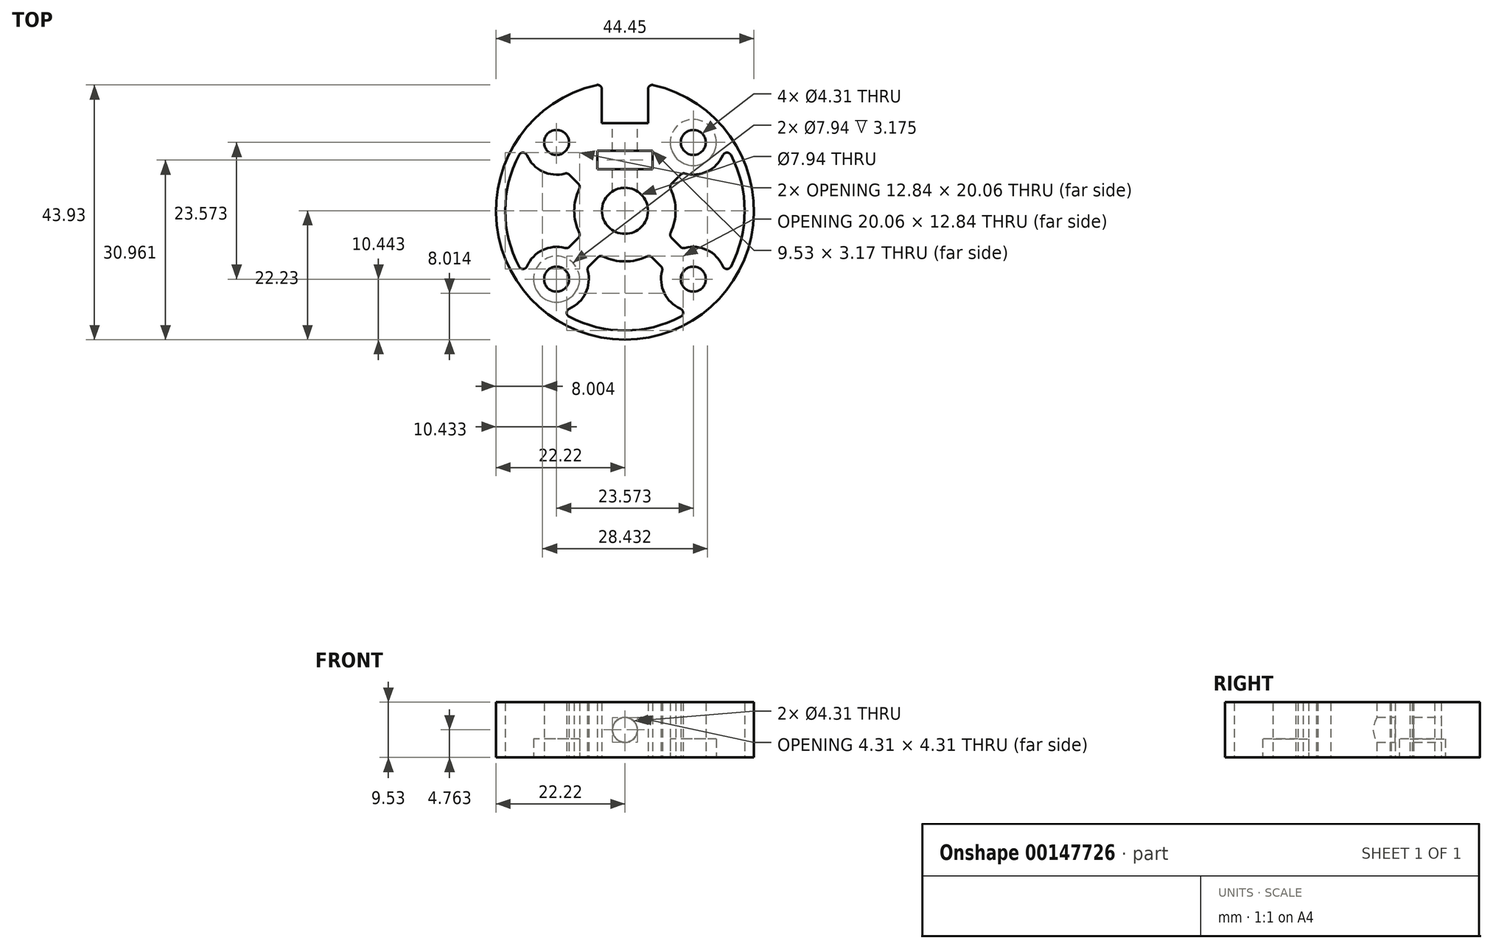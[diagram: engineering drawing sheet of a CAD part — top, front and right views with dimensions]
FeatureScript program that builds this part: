
annotation { "Feature Type Name" : "Feature", "Feature Type Description" : "" }
export const myFeature = defineFeature(function(context is Context, id is Id, definition is map)
    precondition{}
    {
        {
            var Q0;
            Q0=qCreatedBy(makeId("Top.planeOp"),FACE);
            var sketch = newSketch(context, id + "F0", { "sketchPlane" : qUnion([Q0])});
            skCircle(sketch, "E0", {"center": v(0, 0) * mm, "radius": 3.97 * mm});
            skLineSegment(sketch, "E1.bottom", {"start": v(11.79, 11.79) * mm, "end": v(-11.79, 11.79) * mm, "construction": true});
            skLineSegment(sketch, "E1.top", {"start": v(11.79, -11.79) * mm, "end": v(-11.79, -11.79) * mm, "construction": true});
            skLineSegment(sketch, "E1.left", {"start": v(11.79, 11.79) * mm, "end": v(11.79, -11.79) * mm, "construction": true});
            skLineSegment(sketch, "E1.right", {"start": v(-11.79, 11.79) * mm, "end": v(-11.79, -11.79) * mm, "construction": true});
            skCircle(sketch, "E2", {"center": v(-11.79, 11.79) * mm, "radius": 5.56 * mm, "construction": true});
            skLineSegment(sketch, "E3.bottom", {"start": v(-3.97, 21.87) * mm, "end": v(3.97, 21.87) * mm, "construction": true});
            skLineSegment(sketch, "E3.top", {"start": v(-3.97, 15.08) * mm, "end": v(3.97, 15.08) * mm});
            skLineSegment(sketch, "E3.left", {"start": v(-3.97, 21.87) * mm, "end": v(-3.97, 15.08) * mm});
            skLineSegment(sketch, "E3.right", {"start": v(3.97, 21.87) * mm, "end": v(3.97, 15.08) * mm});
            skArc(sketch, "E4", {"start": v(-3.97, 21.87) * mm, "mid": v(0, -22.22) * mm, "end": v(3.97, 21.87) * mm});
            skCircle(sketch, "E5", {"center": v(-11.79, 11.79) * mm, "radius": 2.15 * mm});
            skCircle(sketch, "E6", {"center": v(-11.79, -11.79) * mm, "radius": 2.15 * mm});
            skCircle(sketch, "E7", {"center": v(11.79, -11.79) * mm, "radius": 2.15 * mm});
            skCircle(sketch, "E8", {"center": v(11.79, 11.79) * mm, "radius": 2.15 * mm});
            skLineSegment(sketch, "E9", {"start": v(0, 15.08) * mm, "end": v(0, 10.32) * mm, "construction": true});
            skLineSegment(sketch, "E10", {"start": v(0, 0) * mm, "end": v(0, 2.38) * mm, "construction": true});
            skLineSegment(sketch, "E11", {"start": v(0, 2.38) * mm, "end": v(0, 3.97) * mm, "construction": true});
            skLineSegment(sketch, "E12", {"start": v(0, 3.97) * mm, "end": v(0, 7.14) * mm, "construction": true});
            skLineSegment(sketch, "E13.bottom", {"start": v(4.76, 10.32) * mm, "end": v(-4.76, 10.32) * mm});
            skLineSegment(sketch, "E13.top", {"start": v(4.76, 7.14) * mm, "end": v(-4.76, 7.14) * mm});
            skLineSegment(sketch, "E13.left", {"start": v(4.76, 10.32) * mm, "end": v(4.76, 7.14) * mm});
            skLineSegment(sketch, "E13.right", {"start": v(-4.76, 10.32) * mm, "end": v(-4.76, 7.14) * mm});
            skSolve(sketch);
        }
        {
            var Q0;
            Q0=qSketchRegion(id+"F0",true);
            extrude(context, id + "F1", {"entities" : qUnion([Q0]), "depth" : 9.52 * mm});
        }
        {
            var Q0;
            Q0=makeQuery(id+"F1.opExtrude","SWEPT_FACE",FACE,{"disambiguationData":[OSD([sQuery(id+"F0.wireOp",EDGE,"E3.top")])]});
            var sketch = newSketch(context, id + "F2", { "sketchPlane" : qUnion([Q0])});
            skLineSegment(sketch, "E14", {"start": v(0, 9.53) * mm, "end": v(0, 0) * mm, "construction": true});
            skCircle(sketch, "E15", {"center": v(0, 4.76) * mm, "radius": 2.15 * mm});
            skSolve(sketch);
        }
        {
            var Q0;
            Q0=qSketchRegion(id+"F2",true);
            var Q1;
            Q1=makeQuery(id+"F1.opExtrude","SWEPT_FACE",FACE,{"disambiguationData":[OSD([sQuery(id+"F0.wireOp",EDGE,"E0")])]});
            extrude(context, id + "F3", {"entities" : qUnion([Q0]), "operationType" : NewBodyOperationType.REMOVE, "endBound" : BoundingType.UP_TO_SURFACE, "oppositeDirection" : true, "endBoundEntityFace" : qUnion([Q1]), "depth" : 25.4 * mm});
        }
        {
            var Q0;
            Q0=makeQuery(id+"F1.opExtrude","CAP_FACE",FACE,{"disambiguationData":[OSD([sQuery(id+"F0.wireOp",EDGE,"E0"),sQuery(id+"F0.wireOp",EDGE,"E3.top"),sQuery(id+"F0.wireOp",EDGE,"E3.left"),sQuery(id+"F0.wireOp",EDGE,"E3.right"),sQuery(id+"F0.wireOp",EDGE,"E4"),sQuery(id+"F0.wireOp",EDGE,"E5"),sQuery(id+"F0.wireOp",EDGE,"E6"),sQuery(id+"F0.wireOp",EDGE,"E7"),sQuery(id+"F0.wireOp",EDGE,"E8")])],"isStart":false});
            cPlane(context, id + "F4", {"entities" : qUnion([Q0]), "cplaneType" : CPlaneType.OFFSET, "offset" : 6.35 * mm, "oppositeDirection" : true, "width" : 152.4 * mm, "height" : 152.4 * mm});
        }
        {
            var Q0;
            Q0=makeQuery(id+"F1.opExtrude","CAP_FACE",FACE,{"disambiguationData":[OSD([sQuery(id+"F0.wireOp",EDGE,"E0"),sQuery(id+"F0.wireOp",EDGE,"E3.top"),sQuery(id+"F0.wireOp",EDGE,"E3.left"),sQuery(id+"F0.wireOp",EDGE,"E3.right"),sQuery(id+"F0.wireOp",EDGE,"E4"),sQuery(id+"F0.wireOp",EDGE,"E5"),sQuery(id+"F0.wireOp",EDGE,"E6"),sQuery(id+"F0.wireOp",EDGE,"E7"),sQuery(id+"F0.wireOp",EDGE,"E8")])],"isStart":true});
            var sketch = newSketch(context, id + "F5", { "sketchPlane" : qUnion([Q0])});
            skCircle(sketch, "E16", {"center": v(11.79, -11.79) * mm, "radius": 3.97 * mm});
            skCircle(sketch, "E17", {"center": v(-11.79, 11.79) * mm, "radius": 3.97 * mm});
            skSolve(sketch);
        }
        {
            var Q0;
            Q0=qSketchRegion(id+"F5",true);
            var Q1;
            Q1=qCreatedBy(id+"F4.planeOp",FACE);
            extrude(context, id + "F6", {"entities" : qUnion([Q0]), "operationType" : NewBodyOperationType.REMOVE, "endBound" : BoundingType.UP_TO_SURFACE, "oppositeDirection" : true, "endBoundEntityFace" : qUnion([Q1]), "depth" : 25.4 * mm});
        }
        {
            var Q0;
            Q0=makeQuery(id+"F1.opExtrude","CAP_FACE",FACE,{"disambiguationData":[OSD([sQuery(id+"F0.wireOp",EDGE,"E0"),sQuery(id+"F0.wireOp",EDGE,"E3.top"),sQuery(id+"F0.wireOp",EDGE,"E3.left"),sQuery(id+"F0.wireOp",EDGE,"E3.right"),sQuery(id+"F0.wireOp",EDGE,"E4"),sQuery(id+"F0.wireOp",EDGE,"E5"),sQuery(id+"F0.wireOp",EDGE,"E6"),sQuery(id+"F0.wireOp",EDGE,"E7"),sQuery(id+"F0.wireOp",EDGE,"E8")])],"isStart":true});
            var sketch = newSketch(context, id + "F7", { "sketchPlane" : qUnion([Q0])});
            skArc(sketch, "E18", {"start": v(-9.92, -6.55) * mm, "mid": v(-14.76, -7.1) * mm, "end": v(-17.31, -11.23) * mm});
            skArc(sketch, "E19", {"start": v(-17.31, 11.23) * mm, "mid": v(-14.76, 7.1) * mm, "end": v(-9.92, 6.55) * mm});
            skArc(sketch, "E20", {"start": v(-17.31, 11.23) * mm, "mid": v(-20.64, 0) * mm, "end": v(-17.31, -11.23) * mm});
            skLineSegment(sketch, "E21", {"start": v(-11.79, 11.79) * mm, "end": v(-8.24, 8.24) * mm, "construction": true});
            skLineSegment(sketch, "E22", {"start": v(-11.79, -11.79) * mm, "end": v(-8.24, -8.24) * mm, "construction": true});
            skLineSegment(sketch, "E23", {"start": v(0, 0) * mm, "end": v(-5.94, 5.94) * mm, "construction": true});
            skLineSegment(sketch, "E24", {"start": v(0, 0) * mm, "end": v(-5.94, -5.94) * mm, "construction": true});
            skLineSegment(sketch, "E25.bottom", {"start": v(-7.62, 4.26) * mm, "end": v(-9.92, 6.55) * mm});
            skLineSegment(sketch, "E25.top", {"start": v(-4.26, 7.62) * mm, "end": v(-6.55, 9.92) * mm, "construction": true});
            skLineSegment(sketch, "E25.left", {"start": v(-7.62, 4.26) * mm, "end": v(-4.26, 7.62) * mm, "construction": true});
            skLineSegment(sketch, "E25.right", {"start": v(-9.92, 6.55) * mm, "end": v(-6.55, 9.92) * mm, "construction": true});
            skLineSegment(sketch, "E26.bottom", {"start": v(-7.62, -4.26) * mm, "end": v(-9.92, -6.55) * mm});
            skLineSegment(sketch, "E26.top", {"start": v(-4.26, -7.62) * mm, "end": v(-6.55, -9.92) * mm, "construction": true});
            skLineSegment(sketch, "E26.left", {"start": v(-7.62, -4.26) * mm, "end": v(-4.26, -7.62) * mm, "construction": true});
            skLineSegment(sketch, "E26.right", {"start": v(-9.92, -6.55) * mm, "end": v(-6.55, -9.92) * mm, "construction": true});
            skArc(sketch, "E27", {"start": v(-7.62, 4.26) * mm, "mid": v(-8.73, 0) * mm, "end": v(-7.62, -4.26) * mm});
            skSolve(sketch);
        }
        {
            var Q0;
            Q0=qSketchRegion(id+"F7",true);
            var Q1;
            Q1=makeQuery(id+"F1.opExtrude","CAP_FACE",FACE,{"disambiguationData":[OSD([sQuery(id+"F0.wireOp",EDGE,"E0"),sQuery(id+"F0.wireOp",EDGE,"E3.top"),sQuery(id+"F0.wireOp",EDGE,"E3.left"),sQuery(id+"F0.wireOp",EDGE,"E3.right"),sQuery(id+"F0.wireOp",EDGE,"E4"),sQuery(id+"F0.wireOp",EDGE,"E5"),sQuery(id+"F0.wireOp",EDGE,"E6"),sQuery(id+"F0.wireOp",EDGE,"E7"),sQuery(id+"F0.wireOp",EDGE,"E8")])],"isStart":false});
            extrude(context, id + "F8", {"entities" : qUnion([Q0]), "operationType" : NewBodyOperationType.REMOVE, "endBound" : BoundingType.UP_TO_SURFACE, "oppositeDirection" : true, "endBoundEntityFace" : qUnion([Q1]), "depth" : 25.4 * mm});
        }
        {
            var Q0;
            Q0=makeQuery(id+"F8.boolean.opBoolean","COPY",EDGE,{"derivedFrom":makeQuery(id+"F8.opExtrude","SWEPT_EDGE",EDGE,{"disambiguationData":[OSD([sQuery(id+"F7.wireOp",EDGE,"E19"),sQuery(id+"F7.wireOp",EDGE,"E20")])]})});
            var Q1;
            Q1=makeQuery(id+"F8.boolean.opBoolean","COPY",EDGE,{"derivedFrom":makeQuery(id+"F8.opExtrude","SWEPT_EDGE",EDGE,{"disambiguationData":[OSD([sQuery(id+"F7.wireOp",EDGE,"E19"),sQuery(id+"F7.wireOp",EDGE,"E25.bottom")])]})});
            var Q2;
            Q2=makeQuery(id+"F8.boolean.opBoolean","COPY",EDGE,{"derivedFrom":makeQuery(id+"F8.opExtrude","SWEPT_EDGE",EDGE,{"disambiguationData":[OSD([sQuery(id+"F7.wireOp",EDGE,"E25.bottom"),sQuery(id+"F7.wireOp",EDGE,"E27")])]})});
            var Q3;
            Q3=makeQuery(id+"F8.boolean.opBoolean","COPY",EDGE,{"derivedFrom":makeQuery(id+"F8.opExtrude","SWEPT_EDGE",EDGE,{"disambiguationData":[OSD([sQuery(id+"F7.wireOp",EDGE,"E26.bottom"),sQuery(id+"F7.wireOp",EDGE,"E27")])]})});
            var Q4;
            Q4=makeQuery(id+"F8.boolean.opBoolean","COPY",EDGE,{"derivedFrom":makeQuery(id+"F8.opExtrude","SWEPT_EDGE",EDGE,{"disambiguationData":[OSD([sQuery(id+"F7.wireOp",EDGE,"E18"),sQuery(id+"F7.wireOp",EDGE,"E26.bottom")])]})});
            var Q5;
            Q5=makeQuery(id+"F8.boolean.opBoolean","COPY",EDGE,{"derivedFrom":makeQuery(id+"F8.opExtrude","SWEPT_EDGE",EDGE,{"disambiguationData":[OSD([sQuery(id+"F7.wireOp",EDGE,"E18"),sQuery(id+"F7.wireOp",EDGE,"E20")])]})});
            var Q6;
            Q6=makeQuery(id+"F1.opExtrude","SWEPT_EDGE",EDGE,{"disambiguationData":[OSD([sQuery(id+"F0.wireOp",EDGE,"E3.right"),sQuery(id+"F0.wireOp",EDGE,"E4")])]});
            var Q7;
            Q7=makeQuery(id+"F1.opExtrude","SWEPT_EDGE",EDGE,{"disambiguationData":[OSD([sQuery(id+"F0.wireOp",EDGE,"E3.left"),sQuery(id+"F0.wireOp",EDGE,"E4")])]});
            fillet(context, id + "F9", {"entities" : qUnion([Q0, Q1, Q2, Q3, Q4, Q5, Q6, Q7]), "radius" : 0.76 * mm, "tangentPropagation" : true, "allowEdgeOverflow" : false});
        }
        {
            var Q0;
            Q0=makeQuery(id+"F9.opFillet","BLEND_FACE",FACE,{"disambiguationData":[OSD([sQuery(id+"F7.wireOp",EDGE,"E19"),sQuery(id+"F7.wireOp",EDGE,"E25.bottom")])]});
            var Q1;
            Q1=makeQuery(id+"F8.boolean.opBoolean","COPY",FACE,{"derivedFrom":makeQuery(id+"F8.opExtrude","SWEPT_FACE",FACE,{"disambiguationData":[OSD([sQuery(id+"F7.wireOp",EDGE,"E25.bottom")])]})});
            var Q2;
            Q2=makeQuery(id+"F9.opFillet","BLEND_FACE",FACE,{"disambiguationData":[OSD([sQuery(id+"F7.wireOp",EDGE,"E25.bottom"),sQuery(id+"F7.wireOp",EDGE,"E27")])]});
            var Q3;
            Q3=makeQuery(id+"F8.boolean.opBoolean","COPY",FACE,{"derivedFrom":makeQuery(id+"F8.opExtrude","SWEPT_FACE",FACE,{"disambiguationData":[OSD([sQuery(id+"F7.wireOp",EDGE,"E27")])]})});
            var Q4;
            Q4=makeQuery(id+"F9.opFillet","BLEND_FACE",FACE,{"disambiguationData":[OSD([sQuery(id+"F7.wireOp",EDGE,"E26.bottom"),sQuery(id+"F7.wireOp",EDGE,"E27")])]});
            var Q5;
            Q5=makeQuery(id+"F8.boolean.opBoolean","COPY",FACE,{"derivedFrom":makeQuery(id+"F8.opExtrude","SWEPT_FACE",FACE,{"disambiguationData":[OSD([sQuery(id+"F7.wireOp",EDGE,"E26.bottom")])]})});
            var Q6;
            Q6=makeQuery(id+"F9.opFillet","BLEND_FACE",FACE,{"disambiguationData":[OSD([sQuery(id+"F7.wireOp",EDGE,"E18"),sQuery(id+"F7.wireOp",EDGE,"E26.bottom")])]});
            var Q7;
            Q7=makeQuery(id+"F8.boolean.opBoolean","COPY",FACE,{"derivedFrom":makeQuery(id+"F8.opExtrude","SWEPT_FACE",FACE,{"disambiguationData":[OSD([sQuery(id+"F7.wireOp",EDGE,"E18")])]})});
            var Q8;
            Q8=makeQuery(id+"F9.opFillet","BLEND_FACE",FACE,{"disambiguationData":[OSD([sQuery(id+"F7.wireOp",EDGE,"E18"),sQuery(id+"F7.wireOp",EDGE,"E20")])]});
            var Q9;
            Q9=makeQuery(id+"F8.boolean.opBoolean","COPY",FACE,{"derivedFrom":makeQuery(id+"F8.opExtrude","SWEPT_FACE",FACE,{"disambiguationData":[OSD([sQuery(id+"F7.wireOp",EDGE,"E20")])]})});
            var Q10;
            Q10=makeQuery(id+"F9.opFillet","BLEND_FACE",FACE,{"disambiguationData":[OSD([sQuery(id+"F7.wireOp",EDGE,"E19"),sQuery(id+"F7.wireOp",EDGE,"E20")])]});
            var Q11;
            Q11=makeQuery(id+"F8.boolean.opBoolean","COPY",FACE,{"derivedFrom":makeQuery(id+"F8.opExtrude","SWEPT_FACE",FACE,{"disambiguationData":[OSD([sQuery(id+"F7.wireOp",EDGE,"E19")])]})});
            var Q12;
            Q12=makeQuery(id+"F1.opExtrude","SWEPT_FACE",FACE,{"disambiguationData":[OSD([sQuery(id+"F0.wireOp",EDGE,"E0")])]});
            circularPattern(context, id + "F10", {"patternType" : PatternType.FACE, "faces" : qUnion([Q0, Q1, Q2, Q3, Q4, Q5, Q6, Q7, Q8, Q9, Q10, Q11]), "axis" : qUnion([Q12]), "angle" : 90 * degree, "instanceCount" : 3});
        }
    });
